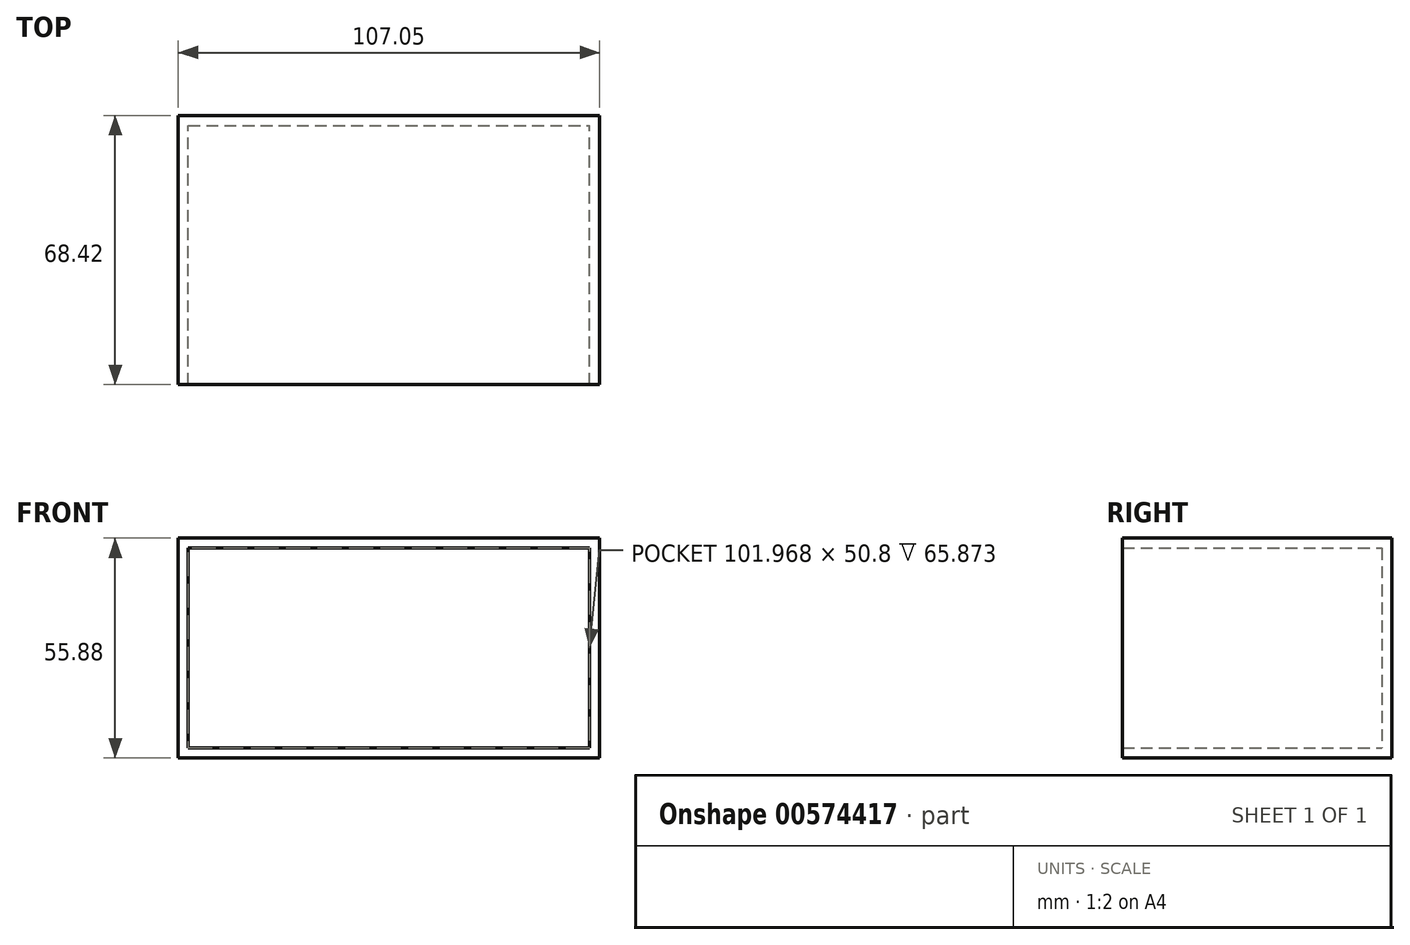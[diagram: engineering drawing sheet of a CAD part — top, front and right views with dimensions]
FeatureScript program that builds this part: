
annotation { "Feature Type Name" : "Feature", "Feature Type Description" : "" }
export const myFeature = defineFeature(function(context is Context, id is Id, definition is map)
    precondition{}
    {
        {
            var Q0;
            Q0=qCreatedBy(makeId("Top.planeOp"),FACE);
            var sketch = newSketch(context, id + "F0", { "sketchPlane" : qUnion([Q0])});
            skLineSegment(sketch, "E0.bottom", {"start": v(-48.13, -33.39) * mm, "end": v(53.84, -33.39) * mm});
            skLineSegment(sketch, "E0.top", {"start": v(-48.13, 32.49) * mm, "end": v(53.84, 32.49) * mm});
            skLineSegment(sketch, "E0.left", {"start": v(-48.13, -33.39) * mm, "end": v(-48.13, 32.49) * mm});
            skLineSegment(sketch, "E0.right", {"start": v(53.84, -33.39) * mm, "end": v(53.84, 32.49) * mm});
            skSolve(sketch);
        }
        {
            var Q0;
            Q0=makeQuery(id+"F0.imprint","IMPRINT",FACE,{"disambiguationData":[TD([[makeQuery(id+"F0.imprint","IMPRINT",EDGE,{"derivedFrom":sQuery(id+"F0.wireOp",EDGE,"E0.bottom")}),1.0]])]});
            extrude(context, id + "F1", {"entities" : qUnion([Q0]), "depth" : 50.8 * mm, "offsetDistance" : 25.4 * mm, "symmetric" : true});
        }
        {
            var Q0;
            Q0=makeQuery(id+"F1.opExtrude","SWEPT_FACE",FACE,{"disambiguationData":[OSD([sQuery(id+"F0.wireOp",EDGE,"E0.bottom")])]});
            shell(context, id + "F2", {"entities" : qUnion([Q0]), "thickness" : 2.54 * mm, "oppositeDirection" : true});
        }
    });
